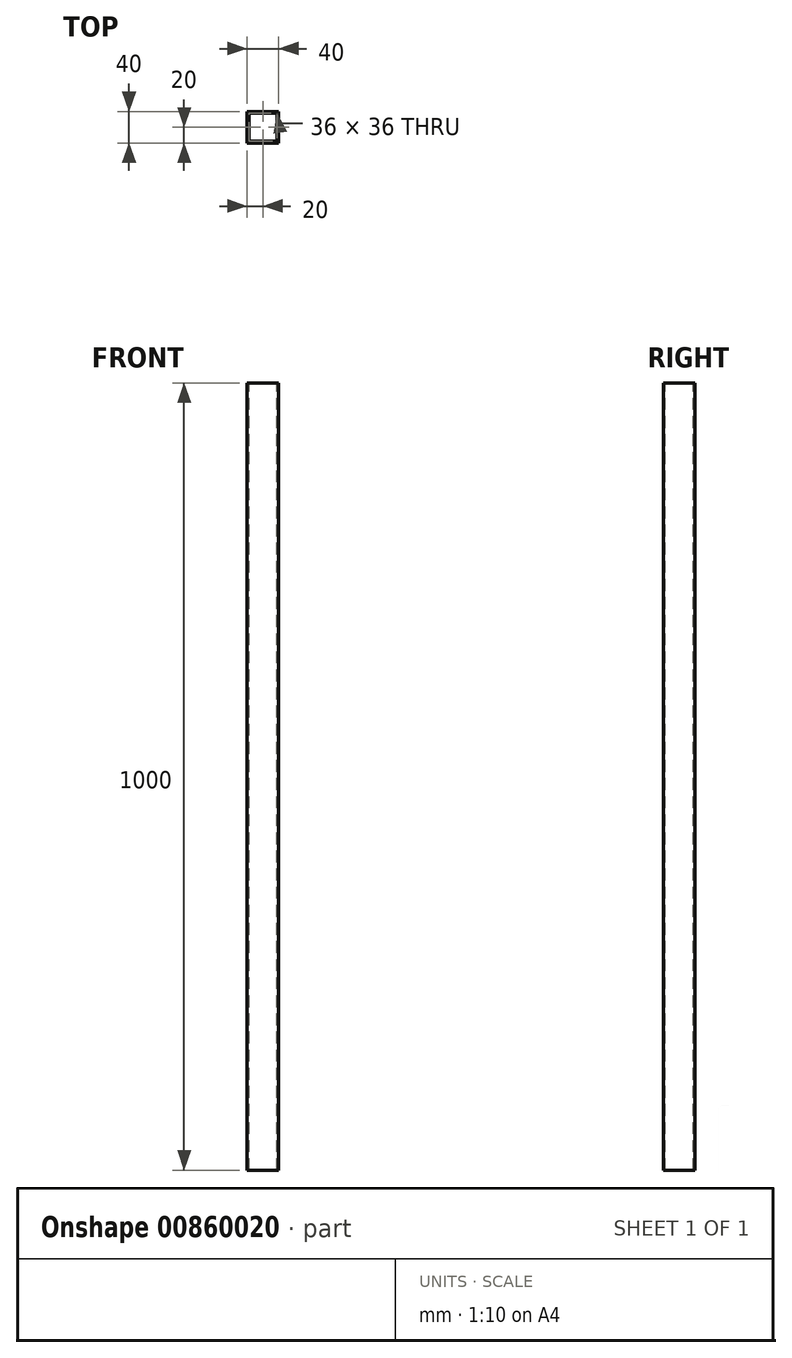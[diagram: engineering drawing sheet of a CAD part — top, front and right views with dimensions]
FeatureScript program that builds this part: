
annotation { "Feature Type Name" : "Feature", "Feature Type Description" : "" }
export const myFeature = defineFeature(function(context is Context, id is Id, definition is map)
    precondition{}
    {
        {
            var Q0;
            Q0=qCreatedBy(makeId("Top.planeOp"),FACE);
            var sketch = newSketch(context, id + "F0", { "sketchPlane" : qUnion([Q0])});
            skLineSegment(sketch, "E0.bottom", {"start": v(20, 20) * mm, "end": v(-20, 20) * mm});
            skLineSegment(sketch, "E0.top", {"start": v(20, -20) * mm, "end": v(-20, -20) * mm});
            skLineSegment(sketch, "E0.left", {"start": v(20, 20) * mm, "end": v(20, -20) * mm});
            skLineSegment(sketch, "E0.right", {"start": v(-20, 20) * mm, "end": v(-20, -20) * mm});
            skPoint(sketch, "E0.middle", {"position": v(0, 0) * mm});
            skSolve(sketch);
        }
        {
            var Q0;
            Q0=makeQuery(id+"F0.imprint","IMPRINT",FACE,{"disambiguationData":[TD([[makeQuery(id+"F0.imprint","IMPRINT",EDGE,{"derivedFrom":sQuery(id+"F0.wireOp",EDGE,"E0.bottom")}),1.0]])]});
            extrude(context, id + "F1", {"entities" : qUnion([Q0]), "depth" : 1000 * mm, "offsetDistance" : 25 * mm});
        }
        {
            var Q0;
            Q0=makeQuery(id+"F1.opExtrude","CAP_FACE",FACE,{"disambiguationData":[OSD([sQuery(id+"F0.wireOp",EDGE,"E0.bottom"),sQuery(id+"F0.wireOp",EDGE,"E0.top"),sQuery(id+"F0.wireOp",EDGE,"E0.left"),sQuery(id+"F0.wireOp",EDGE,"E0.right")])],"isStart":false});
            var sketch = newSketch(context, id + "F2", { "sketchPlane" : qUnion([Q0])});
            skLineSegment(sketch, "E1.bottom", {"start": v(18, 18) * mm, "end": v(-18, 18) * mm});
            skLineSegment(sketch, "E1.top", {"start": v(18, -18) * mm, "end": v(-18, -18) * mm});
            skLineSegment(sketch, "E1.left", {"start": v(18, 18) * mm, "end": v(18, -18) * mm});
            skLineSegment(sketch, "E1.right", {"start": v(-18, 18) * mm, "end": v(-18, -18) * mm});
            skPoint(sketch, "E1.middle", {"position": v(0, 0) * mm});
            skSolve(sketch);
        }
        {
            var Q0;
            Q0=makeQuery(id+"F2.imprint","IMPRINT",FACE,{"disambiguationData":[TD([[makeQuery(id+"F2.imprint","IMPRINT",EDGE,{"derivedFrom":sQuery(id+"F2.wireOp",EDGE,"E1.bottom")}),1.0]])]});
            extrude(context, id + "F3", {"entities" : qUnion([Q0]), "operationType" : NewBodyOperationType.REMOVE, "endBound" : BoundingType.UP_TO_NEXT, "oppositeDirection" : true, "depth" : 25 * mm, "offsetDistance" : 25 * mm});
        }
    });
